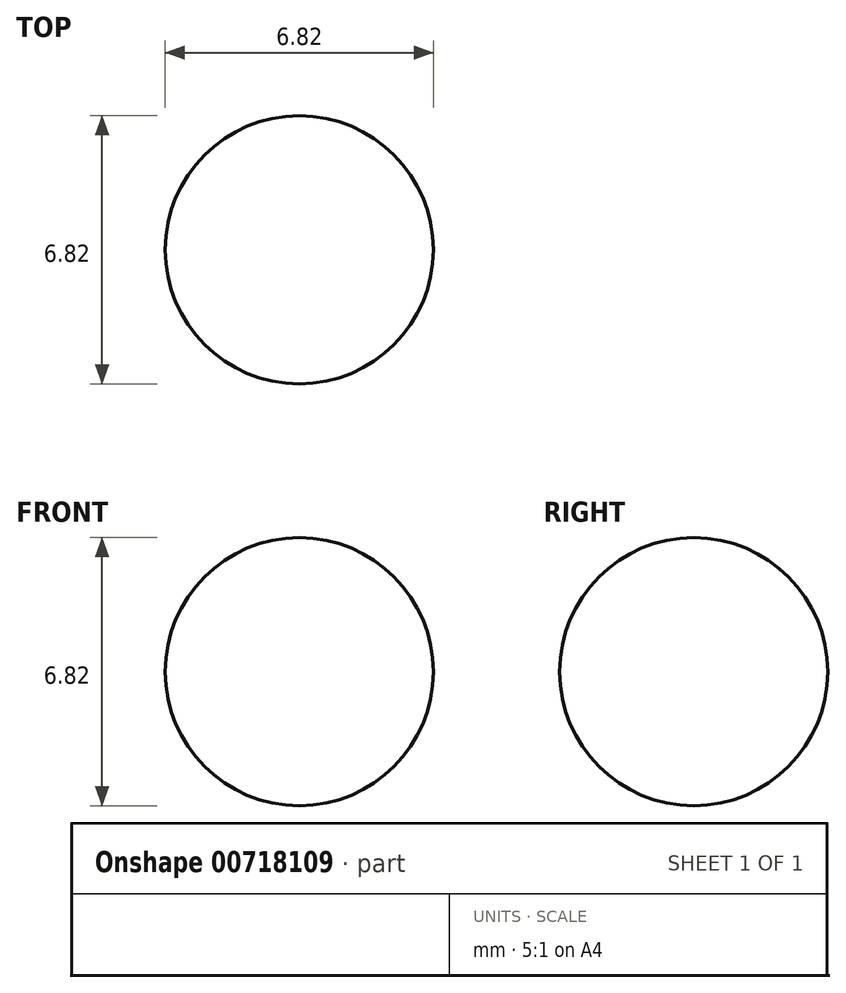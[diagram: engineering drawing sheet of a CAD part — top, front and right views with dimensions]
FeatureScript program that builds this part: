
annotation { "Feature Type Name" : "Feature", "Feature Type Description" : "" }
export const myFeature = defineFeature(function(context is Context, id is Id, definition is map)
    precondition{}
    {
        {
            var Q0;
            Q0=qCreatedBy(makeId("Top.planeOp"),FACE);
            var sketch = newSketch(context, id + "F0", { "sketchPlane" : qUnion([Q0])});
            skCircle(sketch, "E0", {"center": v(0, 0) * mm, "radius": 3.4 * mm});
            skLineSegment(sketch, "E1", {"start": v(0, 3.4) * mm, "end": v(0, -3.4) * mm});
            skSolve(sketch);
        }
        {
            var Q0;
            {var subQ0=sQuery(id+"F0.wireOp",EDGE,"E1");Q0=makeQuery(id+"F0.imprint","IMPRINT",FACE,{"disambiguationData":[TD([[makeQuery(id+"F0.imprint","IMPRINT",EDGE,{"derivedFrom":subQ0}),1.0]])]});}
            var Q1;
            Q1=sQuery(id+"F0.wireOp",EDGE,"E1");
            revolve(context, id + "F1", {"surfaceOperationType" : NewSurfaceOperationType.NEW, "entities" : qUnion([Q0]), "axis" : qUnion([Q1]), "revolveType" : RevolveType.FULL});
        }
    });
